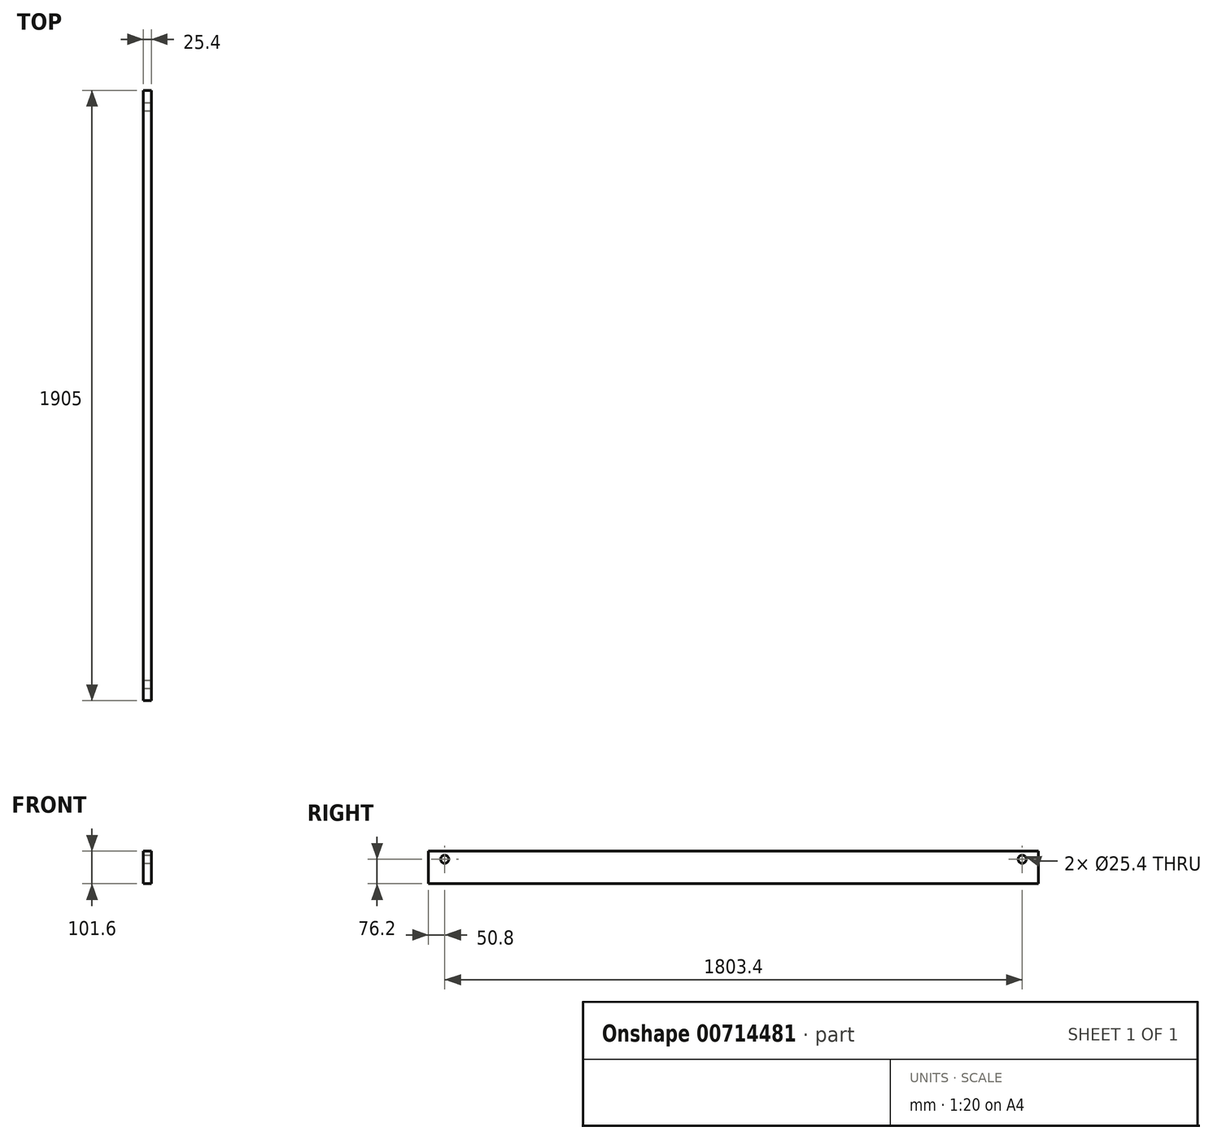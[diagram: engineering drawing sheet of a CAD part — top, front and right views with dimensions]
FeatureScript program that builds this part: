
annotation { "Feature Type Name" : "Feature", "Feature Type Description" : "" }
export const myFeature = defineFeature(function(context is Context, id is Id, definition is map)
    precondition{}
    {
        {
            var Q0;
            Q0=qCreatedBy(makeId("Right.planeOp"),FACE);
            var sketch = newSketch(context, id + "F0", { "sketchPlane" : qUnion([Q0])});
            skLineSegment(sketch, "E0.bottom", {"start": v(1905, 101.6) * mm, "end": v(0, 101.6) * mm});
            skLineSegment(sketch, "E0.top", {"start": v(1905, 0) * mm, "end": v(0, 0) * mm});
            skLineSegment(sketch, "E0.left", {"start": v(1905, 101.6) * mm, "end": v(1905, 0) * mm});
            skLineSegment(sketch, "E0.right", {"start": v(0, 101.6) * mm, "end": v(0, 0) * mm});
            skSolve(sketch);
        }
        {
            var Q0;
            Q0=makeQuery(id+"F0.imprint","IMPRINT",FACE,{"disambiguationData":[TD([[makeQuery(id+"F0.imprint","IMPRINT",EDGE,{"derivedFrom":sQuery(id+"F0.wireOp",EDGE,"E0.bottom")}),1.0]])]});
            extrude(context, id + "F1", {"entities" : qUnion([Q0]), "depth" : 25.4 * mm, "offsetDistance" : 25.4 * mm});
        }
        {
            var Q0;
            Q0=makeQuery(id+"F1.opExtrude","CAP_FACE",FACE,{"disambiguationData":[OSD([sQuery(id+"F0.wireOp",EDGE,"E0.bottom"),sQuery(id+"F0.wireOp",EDGE,"E0.top"),sQuery(id+"F0.wireOp",EDGE,"E0.left"),sQuery(id+"F0.wireOp",EDGE,"E0.right")])],"isStart":false});
            var sketch = newSketch(context, id + "F2", { "sketchPlane" : qUnion([Q0])});
            skLineSegment(sketch, "E1", {"start": v(50.8, 101.6) * mm, "end": v(50.8, 50.8) * mm});
            skLineSegment(sketch, "E2", {"start": v(50.8, 50.8) * mm, "end": v(50.8, 0) * mm});
            skPoint(sketch, "E3", {"position": v(50.8, 25.4) * mm});
            skPoint(sketch, "E4", {"position": v(50.8, 76.2) * mm});
            skCircle(sketch, "E5", {"center": v(50.8, 76.2) * mm, "radius": 12.7 * mm});
            skLineSegment(sketch, "E6", {"start": v(1854.2, 101.6) * mm, "end": v(1854.2, 50.8) * mm});
            skLineSegment(sketch, "E7", {"start": v(1854.2, 50.8) * mm, "end": v(1854.2, 0) * mm});
            skPoint(sketch, "E8", {"position": v(1854.2, 25.4) * mm});
            skPoint(sketch, "E9", {"position": v(1854.2, 76.2) * mm});
            skCircle(sketch, "E10", {"center": v(1854.2, 76.2) * mm, "radius": 12.7 * mm});
            skLineSegment(sketch, "E11", {"start": v(0, 50.8) * mm, "end": v(50.8, 50.8) * mm, "construction": true});
            skLineSegment(sketch, "E12", {"start": v(1905, 50.8) * mm, "end": v(1854.2, 50.8) * mm, "construction": true});
            skSolve(sketch);
        }
        {
            var Q0;
            Q0 = qSketchRegion(id + "F2", true);
            extrude(context, id + "F3", {"entities" : qUnion([Q0]), "operationType" : NewBodyOperationType.REMOVE, "endBound" : BoundingType.THROUGH_ALL, "oppositeDirection" : true, "depth" : 25.4 * mm, "offsetDistance" : 25.4 * mm});
        }
    });
